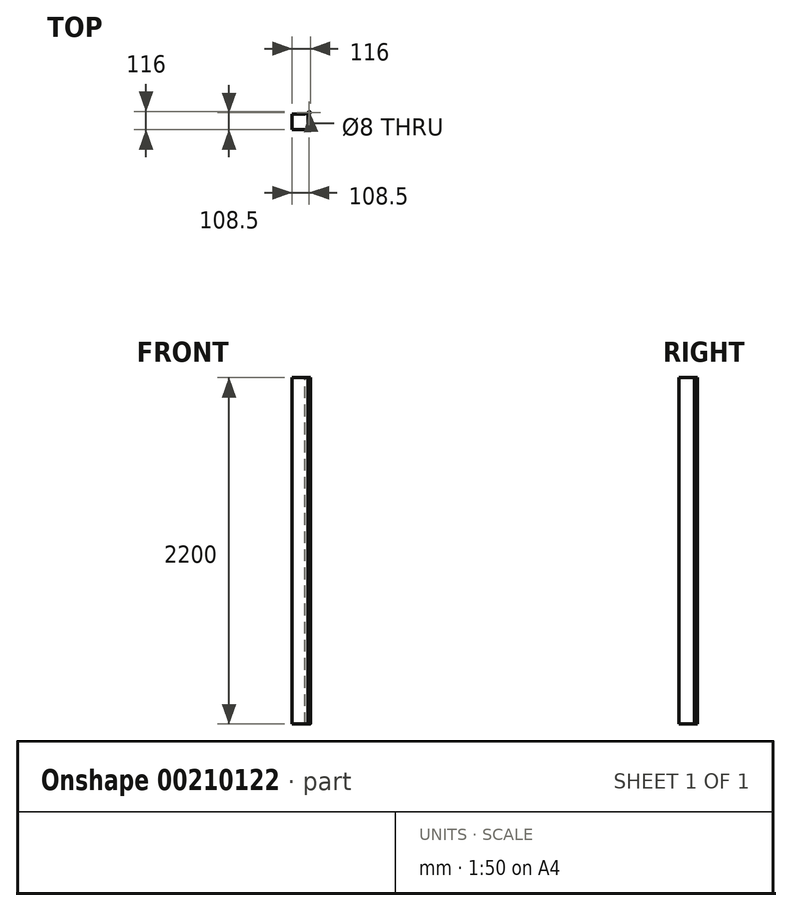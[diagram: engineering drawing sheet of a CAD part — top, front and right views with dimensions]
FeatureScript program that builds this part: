
annotation { "Feature Type Name" : "Feature", "Feature Type Description" : "" }
export const myFeature = defineFeature(function(context is Context, id is Id, definition is map)
    precondition{}
    {
        {
            var Q0;
            Q0=qCreatedBy(makeId("Top.planeOp"),FACE);
            var sketch = newSketch(context, id + "F0", { "sketchPlane" : qUnion([Q0])});
            skLineSegment(sketch, "E0.bottom", {"start": v(50, -50) * mm, "end": v(-50, -50) * mm});
            skLineSegment(sketch, "E0.top", {"start": v(50, 50) * mm, "end": v(-50, 50) * mm});
            skLineSegment(sketch, "E0.left", {"start": v(50, -50) * mm, "end": v(50, 50) * mm});
            skLineSegment(sketch, "E0.right", {"start": v(-50, -50) * mm, "end": v(-50, 50) * mm});
            skPoint(sketch, "E0.middle", {"position": v(0, 0) * mm});
            skSolve(sketch);
        }
        {
            var Q0;
            Q0 = qSketchRegion(id + "F0", true);
            extrude(context, id + "F1", {"entities" : qUnion([Q0]), "depth" : 2200 * mm});
        }
        {
            var Q0;
            Q0=makeQuery(id+"F1.opExtrude","CAP_FACE",FACE,{"disambiguationData":[OSD([sQuery(id+"F0.wireOp",EDGE,"E0.bottom"),sQuery(id+"F0.wireOp",EDGE,"E0.top"),sQuery(id+"F0.wireOp",EDGE,"E0.left"),sQuery(id+"F0.wireOp",EDGE,"E0.right")])],"isStart":false});
            var sketch = newSketch(context, id + "F2", { "sketchPlane" : qUnion([Q0])});
            skCircle(sketch, "E1", {"center": v(58.5, 58.5) * mm, "radius": 7.5 * mm});
            skCircle(sketch, "E2", {"center": v(58.5, 58.5) * mm, "radius": 4 * mm});
            skLineSegment(sketch, "E3", {"start": v(50, 50) * mm, "end": v(59.64, 50) * mm});
            skLineSegment(sketch, "E4", {"start": v(59.64, 50) * mm, "end": v(59.64, 51.09) * mm});
            skLineSegment(sketch, "E5", {"start": v(50, 50) * mm, "end": v(32.7, 50) * mm});
            skLineSegment(sketch, "E6", {"start": v(32.7, 50) * mm, "end": v(32.7, 50.86) * mm});
            skLineSegment(sketch, "E7", {"start": v(32.7, 50.86) * mm, "end": v(56.25, 51.35) * mm});
            skSolve(sketch);
        }
        {
            var Q0;
            Q0 = qSketchRegion(id + "F2", true);
            extrude(context, id + "F3", {"entities" : qUnion([Q0]), "operationType" : NewBodyOperationType.ADD, "oppositeDirection" : true, "depth" : 2200 * mm});
        }
    });
